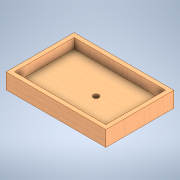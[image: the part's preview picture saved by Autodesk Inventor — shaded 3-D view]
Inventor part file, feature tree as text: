
AUTODESK INVENTOR PART (.ipt)
format: ipt  version: 2020 (Build 240168000, 168)  size: 136,704 bytes
history: native  units: in
note: dims shown in document units (in); Inventor stores cm internally (conversion verified against a paired STEP export)
features: extrude x3, sketch x3
ambient origin geometry x8: Origin, YZ Plane, XZ Plane, XY Plane, X Axis, Y Axis, Z Axis, Center Point
bodies: Body1 (feature_tree)
feature tree (6):
  extrude  "Extrusion3"  Depth=9.5276in
  extrude  "Extrusion7"  Depth=0.7874in
  extrude  "Extrusion8"  Depth=0.5906in
  sketch  "Sketch3"  dims[d4=2.1654in d5=9.5276in]
  sketch  "Sketch7"  dims[d6=13.9764in d7=0.0in d20=0.7874in]
  sketch  "Sketch8"  dims[d21=0.0in d22=0.0in d23=0.5906in d24=0.5906in d25=1.378in d26=0.0in d18=0.1969in d19=0.0344in]
